# Revit family: BIM_KUBAIR F400 CC Pilotair Horizontal
name_source: partatom
category: Equipement de génie climatique
revit_build: Autodesk Revit 2016 (Build: 20161004_0715(x64)
units: mm (PartAtom-declared; Revit-internal decimal feet)

## family parameters
Basée sur le plan de construction = Non
Cote de connecteur circulaire = Utiliser le diamètre
Couper avec des vides une fois chargée = Non
Numéro OmniClass = 23.75.00.00
Partagée = Non
Point de calcul de pièce = Oui
Titre OmniClass = Climate Control (HVAC)
Toujours verticalement = Oui
Type d'élément = Normal

## types (68) — shared parameters
Classe_de_protection_electrique = F
Consignes – raccordements aérauliques = Raccorder 1, 2 ou 3 ouies  au refoulement et 1, 2 ou 3 ouies à l’aspiration
Fabricant = VIM
Hauteur_support = 30 mm  [stored 0.0984252 ft]
IfcExportAs = IfcFan
IfcExportType = IfcFlowMovingDevice
Lien_page_produit = http://www.vim.fr
Materiau_caisson = Acier, galvanisé
Materiau_support = Acier
Protection_IP = IP 55
Visibilité_marque = Oui

## per-type parameters (varying)
| type | A | BH | C | Code_article | Cote_A_capot | Cote_B_capot | Cote_C_capot | Courant_nominal | D | Debit_maxi | Debit_mini | EC | F | Hauteur_pilotair | J | KC | Largeur_pilotair | Modèle | Nombre_de_phases | Poids | Position_V_pilotair | Profondeur_pilotair | Puissance_electrique | Tension_nominale |
| KUBAIR F400 CC 355 4PM DP1M INTZ BDEZ 0,25kW Horizontal | 627 mm  [stored 2.05709 ft] | 695 mm  [stored 2.28018 ft] | 263 mm  [stored 0.862861 ft] | 644535 + 660100 | 340 mm  [stored 1.11549 ft] | 325 mm  [stored 1.06627 ft] | 305 mm  [stored 1.00066 ft] | 3 A | 559 mm  [stored 1.83399 ft] | 3090 m³/h | 900 m³/h | 790 mm | 660 mm  [stored 2.16535 ft] | 214 mm  [stored 0.7021 ft] | 102 mm | 954 mm | 259 mm  [stored 0.849738 ft] | KUBAIR F400 CC 355 4PM DP1M INTZ BDEZ 0,25kW Caisson horizontal | 1 | 59 Kg | 295 mm  [stored 0.967848 ft] | 218 mm  [stored 0.715223 ft] | 250 W | 230 V |
| KUBAIR F400 CC 355 6PM DP1M INTZ BDEZ 0,18kW Horizontal | 627 mm  [stored 2.05709 ft] | 695 mm  [stored 2.28018 ft] | 263 mm  [stored 0.862861 ft] | 644539 + 660100 | 340 mm  [stored 1.11549 ft] | 325 mm  [stored 1.06627 ft] | 305 mm  [stored 1.00066 ft] | 2 A | 559 mm  [stored 1.83399 ft] | 2140 m³/h | 620 m³/h | 790 mm | 660 mm  [stored 2.16535 ft] | 214 mm  [stored 0.7021 ft] | 102 mm | 954 mm | 259 mm  [stored 0.849738 ft] | KUBAIR F400 CC 355 6PM DP1M INTZ BDEZ 0,18kW Caisson horizontal | 1 | 59 Kg | 295 mm  [stored 0.967848 ft] | 218 mm  [stored 0.715223 ft] | 180 W | 230 V |
| KUBAIR F400 CC 355 4PT IE1 DP1V INTZ BDEZ 0,25kW Horizontal | 627 mm  [stored 2.05709 ft] | 695 mm  [stored 2.28018 ft] | 263 mm  [stored 0.862861 ft] | 644543 + 660100 | 340 mm  [stored 1.11549 ft] | 325 mm  [stored 1.06627 ft] | 305 mm  [stored 1.00066 ft] | 1 A | 559 mm  [stored 1.83399 ft] | 3090 m³/h | 900 m³/h | 790 mm | 660 mm  [stored 2.16535 ft] | 214 mm  [stored 0.7021 ft] | 102 mm | 954 mm | 259 mm  [stored 0.849738 ft] | KUBAIR F400 CC 355 4PT IE1 DP1V INTZ BDEZ 0,25kW Caisson horizontal | 3 | 59 Kg | 295 mm  [stored 0.967848 ft] | 218 mm  [stored 0.715223 ft] | 250 W | 400 V |
| KUBAIR F400 CC 355 4PT IE2 DP1V INTZ BDEZ 0,25kW Horizontal | 627 mm  [stored 2.05709 ft] | 695 mm  [stored 2.28018 ft] | 263 mm  [stored 0.862861 ft] | 644547 + 660100 | 340 mm  [stored 1.11549 ft] | 325 mm  [stored 1.06627 ft] | 305 mm  [stored 1.00066 ft] | 1 A | 559 mm  [stored 1.83399 ft] | 3090 m³/h | 900 m³/h | 790 mm | 660 mm  [stored 2.16535 ft] | 214 mm  [stored 0.7021 ft] | 102 mm | 954 mm | 259 mm  [stored 0.849738 ft] | KUBAIR F400 CC 355 4PT IE2 DP1V INTZ BDEZ 0,25kW Caisson horizontal | 3 | 59 Kg | 295 mm  [stored 0.967848 ft] | 218 mm  [stored 0.715223 ft] | 250 W | 400 V |
| KUBAIR F400 CC 355 4PT IE3 DP1V INTZ BDEZ 0,25kW Horizontal | 627 mm  [stored 2.05709 ft] | 695 mm  [stored 2.28018 ft] | 263 mm  [stored 0.862861 ft] | 644551 + 660100 | 340 mm  [stored 1.11549 ft] | 325 mm  [stored 1.06627 ft] | 305 mm  [stored 1.00066 ft] | 1 A | 559 mm  [stored 1.83399 ft] | 3090 m³/h | 900 m³/h | 790 mm | 660 mm  [stored 2.16535 ft] | 214 mm  [stored 0.7021 ft] | 102 mm | 954 mm | 259 mm  [stored 0.849738 ft] | KUBAIR F400 CC 355 4PT IE3 DP1V INTZ BDEZ 0,25kW Caisson horizontal | 3 | 59 Kg | 295 mm  [stored 0.967848 ft] | 218 mm  [stored 0.715223 ft] | 250 W | 400 V |
| KUBAIR F400 CC 355 6PT IE1 DP1V INTZ BDEZ 0,18kW Horizontal | 627 mm  [stored 2.05709 ft] | 695 mm  [stored 2.28018 ft] | 263 mm  [stored 0.862861 ft] | 644555 + 660100 | 340 mm  [stored 1.11549 ft] | 325 mm  [stored 1.06627 ft] | 305 mm  [stored 1.00066 ft] | 1 A | 559 mm  [stored 1.83399 ft] | 2140 m³/h | 620 m³/h | 790 mm | 660 mm  [stored 2.16535 ft] | 214 mm  [stored 0.7021 ft] | 102 mm | 954 mm | 259 mm  [stored 0.849738 ft] | KUBAIR F400 CC 355 6PT IE1 DP1V INTZ BDEZ 0,18kW Caisson horizontal | 3 | 59 Kg | 295 mm  [stored 0.967848 ft] | 218 mm  [stored 0.715223 ft] | 180 W | 400 V |
| KUBAIR F400 CC 355 6PT IE2 DP1V INTZ BDEZ 0,18kW Horizontal | 627 mm  [stored 2.05709 ft] | 695 mm  [stored 2.28018 ft] | 263 mm  [stored 0.862861 ft] | 644559 + 660100 | 340 mm  [stored 1.11549 ft] | 325 mm  [stored 1.06627 ft] | 305 mm  [stored 1.00066 ft] | 1 A | 559 mm  [stored 1.83399 ft] | 2140 m³/h | 620 m³/h | 790 mm | 660 mm  [stored 2.16535 ft] | 214 mm  [stored 0.7021 ft] | 102 mm | 954 mm | 259 mm  [stored 0.849738 ft] | KUBAIR F400 CC 355 6PT IE2 DP1V INTZ BDEZ 0,18kW Caisson horizontal | 3 | 59 Kg | 295 mm  [stored 0.967848 ft] | 218 mm  [stored 0.715223 ft] | 180 W | 400 V |
| KUBAIR F400 CC 355 6PT IE3 DP1V INTZ BDEZ 0,18kW Horizontal | 627 mm  [stored 2.05709 ft] | 695 mm  [stored 2.28018 ft] | 263 mm  [stored 0.862861 ft] | 644563 + 660100 | 340 mm  [stored 1.11549 ft] | 325 mm  [stored 1.06627 ft] | 305 mm  [stored 1.00066 ft] | 1 A | 559 mm  [stored 1.83399 ft] | 2140 m³/h | 620 m³/h | 790 mm | 660 mm  [stored 2.16535 ft] | 214 mm  [stored 0.7021 ft] | 102 mm | 954 mm | 259 mm  [stored 0.849738 ft] | KUBAIR F400 CC 355 6PT IE3 DP1V INTZ BDEZ 0,18kW Caisson horizontal | 3 | 59 Kg | 295 mm  [stored 0.967848 ft] | 218 mm  [stored 0.715223 ft] | 180 W | 400 V |
| KUBAIR F400 CC 400 4PM DP1M INTZ BDEZ 0,55kW Horizontal | 699 mm  [stored 2.29331 ft] | 767 mm  [stored 2.5164 ft] | 297 mm  [stored 0.974409 ft] | 644575 + 660101 | 340 mm  [stored 1.11549 ft] | 325 mm  [stored 1.06627 ft] | 305 mm  [stored 1.00066 ft] | 4 A | 631 mm  [stored 2.07021 ft] | 5000 m³/h | 1060 m³/h | 864 mm | 732 mm | 214 mm  [stored 0.7021 ft] | 102 mm | 1022 mm | 259 mm  [stored 0.849738 ft] | KUBAIR F400 CC 400 4PM DP1M INTZ BDEZ 0,55kW Caisson horizontal | 1 | 72 Kg | 295 mm  [stored 0.967848 ft] | 218 mm  [stored 0.715223 ft] | 550 W | 230 V |
| KUBAIR F400 CC 400 6PM DP1M INTZ BDEZ 0,25kW Horizontal | 699 mm  [stored 2.29331 ft] | 767 mm  [stored 2.5164 ft] | 297 mm  [stored 0.974409 ft] | 644579 + 660101 | 340 mm  [stored 1.11549 ft] | 325 mm  [stored 1.06627 ft] | 305 mm  [stored 1.00066 ft] | 2 A | 631 mm  [stored 2.07021 ft] | 3310 m³/h | 520 m³/h | 864 mm | 732 mm | 214 mm  [stored 0.7021 ft] | 102 mm | 1022 mm | 259 mm  [stored 0.849738 ft] | KUBAIR F400 CC 400 6PM DP1M INTZ BDEZ 0,25kW Caisson horizontal | 1 | 72 Kg | 295 mm  [stored 0.967848 ft] | 218 mm  [stored 0.715223 ft] | 250 W | 230 V |
| KUBAIR F400 CC 400 4PT IE1 DP1V INTZ BDEZ 0,55kW Horizontal | 699 mm  [stored 2.29331 ft] | 767 mm  [stored 2.5164 ft] | 297 mm  [stored 0.974409 ft] | 644583 + 660101 | 340 mm  [stored 1.11549 ft] | 325 mm  [stored 1.06627 ft] | 305 mm  [stored 1.00066 ft] | 1 A | 631 mm  [stored 2.07021 ft] | 5000 m³/h | 1060 m³/h | 864 mm | 732 mm | 214 mm  [stored 0.7021 ft] | 102 mm | 1022 mm | 259 mm  [stored 0.849738 ft] | KUBAIR F400 CC 400 4PT IE1 DP1V INTZ BDEZ 0,55kW Caisson horizontal | 3 | 72 Kg | 295 mm  [stored 0.967848 ft] | 218 mm  [stored 0.715223 ft] | 550 W | 400 V |
| KUBAIR F400 CC 400 4PT IE2 DP1V INTZ BDEZ 0,55kW Horizontal | 699 mm  [stored 2.29331 ft] | 767 mm  [stored 2.5164 ft] | 297 mm  [stored 0.974409 ft] | 644587 + 660101 | 340 mm  [stored 1.11549 ft] | 325 mm  [stored 1.06627 ft] | 305 mm  [stored 1.00066 ft] | 1 A | 631 mm  [stored 2.07021 ft] | 5000 m³/h | 1060 m³/h | 864 mm | 732 mm | 214 mm  [stored 0.7021 ft] | 102 mm | 1022 mm | 259 mm  [stored 0.849738 ft] | KUBAIR F400 CC 400 4PT IE2 DP1V INTZ BDEZ 0,55kW Caisson horizontal | 3 | 72 Kg | 295 mm  [stored 0.967848 ft] | 218 mm  [stored 0.715223 ft] | 550 W | 400 V |
| KUBAIR F400 CC 400 4PT IE3 DP1V INTZ BDEZ 0,55kW Horizontal | 699 mm  [stored 2.29331 ft] | 767 mm  [stored 2.5164 ft] | 297 mm  [stored 0.974409 ft] | 644591 + 660101 | 340 mm  [stored 1.11549 ft] | 325 mm  [stored 1.06627 ft] | 305 mm  [stored 1.00066 ft] | 1 A | 631 mm  [stored 2.07021 ft] | 5000 m³/h | 1060 m³/h | 864 mm | 732 mm | 214 mm  [stored 0.7021 ft] | 102 mm | 1022 mm | 259 mm  [stored 0.849738 ft] | KUBAIR F400 CC 400 4PT IE3 DP1V INTZ BDEZ 0,55kW Caisson horizontal | 3 | 72 Kg | 295 mm  [stored 0.967848 ft] | 218 mm  [stored 0.715223 ft] | 550 W | 400 V |
| KUBAIR F400 CC 400 6PT IE1 DP1V INTZ BDEZ 0,37kW Horizontal | 699 mm  [stored 2.29331 ft] | 767 mm  [stored 2.5164 ft] | 297 mm  [stored 0.974409 ft] | 644595 + 660101 | 340 mm  [stored 1.11549 ft] | 325 mm  [stored 1.06627 ft] | 305 mm  [stored 1.00066 ft] | 1 A | 631 mm  [stored 2.07021 ft] | 3310 m³/h | 520 m³/h | 864 mm | 732 mm | 214 mm  [stored 0.7021 ft] | 102 mm | 1022 mm | 259 mm  [stored 0.849738 ft] | KUBAIR F400 CC 400 6PT IE1 DP1V INTZ BDEZ 0,37kW Caisson horizontal | 3 | 72 Kg | 295 mm  [stored 0.967848 ft] | 218 mm  [stored 0.715223 ft] | 370 W | 400 V |
| KUBAIR F400 CC 400 6PT IE2 DP1V INTZ BDEZ 0,37kW Horizontal | 699 mm  [stored 2.29331 ft] | 767 mm  [stored 2.5164 ft] | 297 mm  [stored 0.974409 ft] | 644599 + 660101 | 340 mm  [stored 1.11549 ft] | 325 mm  [stored 1.06627 ft] | 305 mm  [stored 1.00066 ft] | 1 A | 631 mm  [stored 2.07021 ft] | 3310 m³/h | 520 m³/h | 864 mm | 732 mm | 214 mm  [stored 0.7021 ft] | 102 mm | 1022 mm | 259 mm  [stored 0.849738 ft] | KUBAIR F400 CC 400 6PT IE2 DP1V INTZ BDEZ 0,37kW Caisson horizontal | 3 | 72 Kg | 295 mm  [stored 0.967848 ft] | 218 mm  [stored 0.715223 ft] | 370 W | 400 V |
| KUBAIR F400 CC 400 6PT IE3 DP1V INTZ BDEZ 0,37kW Horizontal | 699 mm  [stored 2.29331 ft] | 767 mm  [stored 2.5164 ft] | 297 mm  [stored 0.974409 ft] | 644603 + 660101 | 340 mm  [stored 1.11549 ft] | 325 mm  [stored 1.06627 ft] | 305 mm  [stored 1.00066 ft] | 1 A | 631 mm  [stored 2.07021 ft] | 3310 m³/h | 520 m³/h | 864 mm | 732 mm | 214 mm  [stored 0.7021 ft] | 102 mm | 1022 mm | 259 mm  [stored 0.849738 ft] | KUBAIR F400 CC 400 6PT IE3 DP1V INTZ BDEZ 0,37kW Caisson horizontal | 3 | 72 Kg | 295 mm  [stored 0.967848 ft] | 218 mm  [stored 0.715223 ft] | 370 W | 400 V |
| KUBAIR F400 CC 450 6PM DP1M INTZ BDEZ 0,25kW Horizontal | 779 mm | 847 mm | 326 mm  [stored 1.06955 ft] | 644615 + 660102 | 340 mm  [stored 1.11549 ft] | 325 mm  [stored 1.06627 ft] | 305 mm  [stored 1.00066 ft] | 2 A | 711 mm  [stored 2.33268 ft] | 4750 m³/h | 820 m³/h | 990 mm | 812 mm | 214 mm  [stored 0.7021 ft] | 102 mm | 1081 mm | 259 mm  [stored 0.849738 ft] | KUBAIR F400 CC 450 6PM DP1M INTZ BDEZ 0,25kW Caisson horizontal | 1 | 92 Kg | 295 mm  [stored 0.967848 ft] | 218 mm  [stored 0.715223 ft] | 250 W | 230 V |
| KUBAIR F400 CC 450 4PT IE2 DP1V INTZ BDEZ 1,1kW Horizontal | 779 mm | 847 mm | 326 mm  [stored 1.06955 ft] | 644619 + 660102 | 340 mm  [stored 1.11549 ft] | 325 mm  [stored 1.06627 ft] | 305 mm  [stored 1.00066 ft] | 2 A | 711 mm  [stored 2.33268 ft] | 7080 m³/h | 1230 m³/h | 990 mm | 812 mm | 214 mm  [stored 0.7021 ft] | 102 mm | 1081 mm | 259 mm  [stored 0.849738 ft] | KUBAIR F400 CC 450 4PT IE2 DP1V INTZ BDEZ 1,1kW Caisson horizontal | 3 | 92 Kg | 295 mm  [stored 0.967848 ft] | 218 mm  [stored 0.715223 ft] | 1100 W | 400 V |
| KUBAIR F400 CC 450 4PT IE3 DP1V INTZ BDEZ 1,1kW Horizontal | 779 mm | 847 mm | 326 mm  [stored 1.06955 ft] | 644623 + 660102 | 340 mm  [stored 1.11549 ft] | 325 mm  [stored 1.06627 ft] | 305 mm  [stored 1.00066 ft] | 2 A | 711 mm  [stored 2.33268 ft] | 7080 m³/h | 1230 m³/h | 990 mm | 812 mm | 214 mm  [stored 0.7021 ft] | 102 mm | 1081 mm | 259 mm  [stored 0.849738 ft] | KUBAIR F400 CC 450 4PT IE3 DP1V INTZ BDEZ 1,1kW Caisson horizontal | 3 | 92 Kg | 295 mm  [stored 0.967848 ft] | 218 mm  [stored 0.715223 ft] | 1100 W | 400 V |
| KUBAIR F400 CC 450 6PT IE1 DP1V INTZ BDEZ 0,37kW Horizontal | 779 mm | 847 mm | 326 mm  [stored 1.06955 ft] | 644627 + 660102 | 340 mm  [stored 1.11549 ft] | 325 mm  [stored 1.06627 ft] | 305 mm  [stored 1.00066 ft] | 1 A | 711 mm  [stored 2.33268 ft] | 4750 m³/h | 820 m³/h | 990 mm | 812 mm | 214 mm  [stored 0.7021 ft] | 102 mm | 1081 mm | 259 mm  [stored 0.849738 ft] | KUBAIR F400 CC 450 6PT IE1 DP1V INTZ BDEZ 0,37kW Caisson horizontal | 3 | 92 Kg | 295 mm  [stored 0.967848 ft] | 218 mm  [stored 0.715223 ft] | 370 W | 400 V |
| KUBAIR F400 CC 450 6PT IE2 DP1V INTZ BDEZ 0,37kW Horizontal | 779 mm | 847 mm | 326 mm  [stored 1.06955 ft] | 644631 + 660102 | 340 mm  [stored 1.11549 ft] | 325 mm  [stored 1.06627 ft] | 305 mm  [stored 1.00066 ft] | 1 A | 711 mm  [stored 2.33268 ft] | 4750 m³/h | 820 m³/h | 990 mm | 812 mm | 214 mm  [stored 0.7021 ft] | 102 mm | 1081 mm | 259 mm  [stored 0.849738 ft] | KUBAIR F400 CC 450 6PT IE2 DP1V INTZ BDEZ 0,37kW Caisson horizontal | 3 | 92 Kg | 295 mm  [stored 0.967848 ft] | 218 mm  [stored 0.715223 ft] | 370 W | 400 V |
| KUBAIR F400 CC 450 6PT IE3 DP1V INTZ BDEZ 0,37kW Horizontal | 779 mm | 847 mm | 326 mm  [stored 1.06955 ft] | 644635 + 660102 | 340 mm  [stored 1.11549 ft] | 325 mm  [stored 1.06627 ft] | 305 mm  [stored 1.00066 ft] | 1 A | 711 mm  [stored 2.33268 ft] | 4750 m³/h | 820 m³/h | 990 mm | 812 mm | 214 mm  [stored 0.7021 ft] | 102 mm | 1081 mm | 259 mm  [stored 0.849738 ft] | KUBAIR F400 CC 450 6PT IE3 DP1V INTZ BDEZ 0,37kW Caisson horizontal | 3 | 92 Kg | 295 mm  [stored 0.967848 ft] | 218 mm  [stored 0.715223 ft] | 370 W | 400 V |
| KUBAIR F400 CC 450 8PT IE1 DP1V INTZ BDEZ 0,18kW Horizontal | 779 mm | 847 mm | 326 mm  [stored 1.06955 ft] | 644639 + 660102 | 340 mm  [stored 1.11549 ft] | 325 mm  [stored 1.06627 ft] | 305 mm  [stored 1.00066 ft] | 1 A | 711 mm  [stored 2.33268 ft] | 3420 m³/h | 590 m³/h | 990 mm | 812 mm | 214 mm  [stored 0.7021 ft] | 102 mm | 1081 mm | 259 mm  [stored 0.849738 ft] | KUBAIR F400 CC 450 8PT IE1 DP1V INTZ BDEZ 0,18kW Caisson horizontal | 3 | 92 Kg | 295 mm  [stored 0.967848 ft] | 218 mm  [stored 0.715223 ft] | 180 W | 400 V |
| KUBAIR F400 CC 450 8PT IE2 DP1V INTZ BDEZ 0,18kW Horizontal | 779 mm | 847 mm | 326 mm  [stored 1.06955 ft] | 644643 + 660102 | 340 mm  [stored 1.11549 ft] | 325 mm  [stored 1.06627 ft] | 305 mm  [stored 1.00066 ft] | 1 A | 711 mm  [stored 2.33268 ft] | 3420 m³/h | 590 m³/h | 990 mm | 812 mm | 214 mm  [stored 0.7021 ft] | 102 mm | 1081 mm | 259 mm  [stored 0.849738 ft] | KUBAIR F400 CC 450 8PT IE2 DP1V INTZ BDEZ 0,18kW Caisson horizontal | 3 | 92 Kg | 295 mm  [stored 0.967848 ft] | 218 mm  [stored 0.715223 ft] | 180 W | 400 V |
| KUBAIR F400 CC 450 8PT IE3 DP1V INTZ BDEZ 0,18kW Horizontal | 779 mm | 847 mm | 326 mm  [stored 1.06955 ft] | 644647 + 660102 | 340 mm  [stored 1.11549 ft] | 325 mm  [stored 1.06627 ft] | 305 mm  [stored 1.00066 ft] | 1 A | 711 mm  [stored 2.33268 ft] | 3420 m³/h | 590 m³/h | 990 mm | 812 mm | 214 mm  [stored 0.7021 ft] | 102 mm | 1081 mm | 259 mm  [stored 0.849738 ft] | KUBAIR F400 CC 450 8PT IE3 DP1V INTZ BDEZ 0,18kW Caisson horizontal | 3 | 92 Kg | 295 mm  [stored 0.967848 ft] | 218 mm  [stored 0.715223 ft] | 180 W | 400 V |
| KUBAIR F400 CC 500 6PM DP1M INTZ BDEZ 0,37kW Horizontal | 858 mm | 925 mm | 338 mm  [stored 1.10892 ft] | 644663 + 660103 | 415 mm | 475 mm | 355 mm  [stored 1.1647 ft] | 3 A | 768 mm  [stored 2.51969 ft] | 5960 m³/h | 920 m³/h | 1039 mm | 890 mm | 214 mm  [stored 0.7021 ft] | 112 mm  [stored 0.367454 ft] | 1145 mm | 259 mm  [stored 0.849738 ft] | KUBAIR F400 CC 500 6PM DP1M INTZ BDEZ 0,37kW Caisson horizontal | 1 | 114 Kg | 303 mm | 218 mm  [stored 0.715223 ft] | 370 W | 230 V |
| KUBAIR F400 CC 500 4PT IE2 DP1V INTZ BDEZ 1,5kW Horizontal | 858 mm | 925 mm | 338 mm  [stored 1.10892 ft] | 644667 + 660103 | 415 mm | 475 mm | 355 mm  [stored 1.1647 ft] | 3 A | 768 mm  [stored 2.51969 ft] | 8850 m³/h | 1370 m³/h | 1039 mm | 890 mm | 214 mm  [stored 0.7021 ft] | 112 mm  [stored 0.367454 ft] | 1145 mm | 259 mm  [stored 0.849738 ft] | KUBAIR F400 CC 500 4PT IE2 DP1V INTZ BDEZ 1,5kW Caisson horizontal | 3 | 114 Kg | 303 mm | 218 mm  [stored 0.715223 ft] | 1500 W | 400 V |
| KUBAIR F400 CC 500 4PT IE3 DP1V INTZ BDEZ 1,5kW Horizontal | 858 mm | 925 mm | 338 mm  [stored 1.10892 ft] | 644671 + 660103 | 415 mm | 475 mm | 355 mm  [stored 1.1647 ft] | 3 A | 768 mm  [stored 2.51969 ft] | 8850 m³/h | 1370 m³/h | 1039 mm | 890 mm | 214 mm  [stored 0.7021 ft] | 112 mm  [stored 0.367454 ft] | 1145 mm | 259 mm  [stored 0.849738 ft] | KUBAIR F400 CC 500 4PT IE3 DP1V INTZ BDEZ 1,5kW Caisson horizontal | 3 | 114 Kg | 303 mm | 218 mm  [stored 0.715223 ft] | 1500 W | 400 V |
| KUBAIR F400 CC 500 6PT IE1 DP1V INTZ BDEZ 0,55kW Horizontal | 858 mm | 925 mm | 338 mm  [stored 1.10892 ft] | 644675 + 660103 | 415 mm | 475 mm | 355 mm  [stored 1.1647 ft] | 2 A | 768 mm  [stored 2.51969 ft] | 5960 m³/h | 920 m³/h | 1039 mm | 890 mm | 214 mm  [stored 0.7021 ft] | 112 mm  [stored 0.367454 ft] | 1145 mm | 259 mm  [stored 0.849738 ft] | KUBAIR F400 CC 500 6PT IE1 DP1V INTZ BDEZ 0,55kW Caisson horizontal | 3 | 114 Kg | 303 mm | 218 mm  [stored 0.715223 ft] | 550 W | 400 V |
| KUBAIR F400 CC 500 6PT IE2 DP1V INTZ BDEZ 0,55kW Horizontal | 858 mm | 925 mm | 338 mm  [stored 1.10892 ft] | 644679 + 660103 | 415 mm | 475 mm | 355 mm  [stored 1.1647 ft] | 1 A | 768 mm  [stored 2.51969 ft] | 5960 m³/h | 920 m³/h | 1039 mm | 890 mm | 214 mm  [stored 0.7021 ft] | 112 mm  [stored 0.367454 ft] | 1145 mm | 259 mm  [stored 0.849738 ft] | KUBAIR F400 CC 500 6PT IE2 DP1V INTZ BDEZ 0,55kW Caisson horizontal | 3 | 114 Kg | 303 mm | 218 mm  [stored 0.715223 ft] | 550 W | 400 V |
| KUBAIR F400 CC 500 6PT IE3 DP1V INTZ BDEZ 0,55kW Horizontal | 858 mm | 925 mm | 338 mm  [stored 1.10892 ft] | 644683 + 660103 | 415 mm | 475 mm | 355 mm  [stored 1.1647 ft] | 1 A | 768 mm  [stored 2.51969 ft] | 5960 m³/h | 920 m³/h | 1039 mm | 890 mm | 214 mm  [stored 0.7021 ft] | 112 mm  [stored 0.367454 ft] | 1145 mm | 259 mm  [stored 0.849738 ft] | KUBAIR F400 CC 500 6PT IE3 DP1V INTZ BDEZ 0,55kW Caisson horizontal | 3 | 114 Kg | 303 mm | 218 mm  [stored 0.715223 ft] | 550 W | 400 V |
| KUBAIR F400 CC 500 8PT IE1 DP1V INTZ BDEZ 0,18kW Horizontal | 858 mm | 925 mm | 338 mm  [stored 1.10892 ft] | 644687 + 660103 | 415 mm | 475 mm | 355 mm  [stored 1.1647 ft] | 1 A | 768 mm  [stored 2.51969 ft] | 4280 m³/h | 660 m³/h | 1039 mm | 890 mm | 214 mm  [stored 0.7021 ft] | 112 mm  [stored 0.367454 ft] | 1145 mm | 259 mm  [stored 0.849738 ft] | KUBAIR F400 CC 500 8PT IE1 DP1V INTZ BDEZ 0,18kW Caisson horizontal | 3 | 114 Kg | 303 mm | 218 mm  [stored 0.715223 ft] | 180 W | 400 V |
| KUBAIR F400 CC 500 8PT IE2 DP1V INTZ BDEZ 0,18kW Horizontal | 858 mm | 925 mm | 338 mm  [stored 1.10892 ft] | 644691 + 660103 | 415 mm | 475 mm | 355 mm  [stored 1.1647 ft] | 1 A | 768 mm  [stored 2.51969 ft] | 4280 m³/h | 660 m³/h | 1039 mm | 890 mm | 214 mm  [stored 0.7021 ft] | 112 mm  [stored 0.367454 ft] | 1145 mm | 259 mm  [stored 0.849738 ft] | KUBAIR F400 CC 500 8PT IE2 DP1V INTZ BDEZ 0,18kW Caisson horizontal | 3 | 114 Kg | 303 mm | 218 mm  [stored 0.715223 ft] | 180 W | 400 V |
| KUBAIR F400 CC 500 8PT IE3 DP1V INTZ BDEZ 0,18kW Horizontal | 858 mm | 925 mm | 338 mm  [stored 1.10892 ft] | 644695 + 660103 | 415 mm | 475 mm | 355 mm  [stored 1.1647 ft] | 1 A | 768 mm  [stored 2.51969 ft] | 4280 m³/h | 660 m³/h | 1039 mm | 890 mm | 214 mm  [stored 0.7021 ft] | 112 mm  [stored 0.367454 ft] | 1145 mm | 259 mm  [stored 0.849738 ft] | KUBAIR F400 CC 500 8PT IE3 DP1V INTZ BDEZ 0,18kW Caisson horizontal | 3 | 114 Kg | 303 mm | 218 mm  [stored 0.715223 ft] | 180 W | 400 V |
| KUBAIR F400 CC 500 4/6PT DP2I INTZ BDEZ 1,50/0,37kW Horizontal | 858 mm | 925 mm | 338 mm  [stored 1.10892 ft] | 644699 + 660103 | 415 mm | 475 mm | 355 mm  [stored 1.1647 ft] | 4 A | 768 mm  [stored 2.51969 ft] | 8850 m³/h | 1370 m³/h | 1039 mm | 890 mm | 214 mm  [stored 0.7021 ft] | 112 mm  [stored 0.367454 ft] | 1145 mm | 259 mm  [stored 0.849738 ft] | KUBAIR F400 CC 500 4/6PT DP2I INTZ BDEZ 1,50/0,37kW Caisson horizontal | 3 | 116 Kg | 303 mm | 218 mm  [stored 0.715223 ft] | 1500 W | 400 V |
| KUBAIR F400 CC 500 4/8PT DP2D INTZ BDEZ 1,60/0,40kW Horizontal | 858 mm | 925 mm | 338 mm  [stored 1.10892 ft] | 644703 + 660103 | 415 mm | 475 mm | 355 mm  [stored 1.1647 ft] | 4 A | 768 mm  [stored 2.51969 ft] | 8850 m³/h | 1370 m³/h | 1039 mm | 890 mm | 214 mm  [stored 0.7021 ft] | 112 mm  [stored 0.367454 ft] | 1145 mm | 259 mm  [stored 0.849738 ft] | KUBAIR F400 CC 500 4/8PT DP2D INTZ BDEZ 1,60/0,40kW Caisson horizontal | 3 | 116 Kg | 303 mm | 218 mm  [stored 0.715223 ft] | 1600 W | 400 V |
| KUBAIR F400 CC 500 6/8PT DP2I INTZ BDEZ 0,55/0,37kW Horizontal | 858 mm | 925 mm | 338 mm  [stored 1.10892 ft] | 644707 + 660103 | 415 mm | 475 mm | 355 mm  [stored 1.1647 ft] | 2 A | 768 mm  [stored 2.51969 ft] | 5960 m³/h | 920 m³/h | 1039 mm | 890 mm | 214 mm  [stored 0.7021 ft] | 112 mm  [stored 0.367454 ft] | 1145 mm | 259 mm  [stored 0.849738 ft] | KUBAIR F400 CC 500 6/8PT DP2I INTZ BDEZ 0,55/0,37kW Caisson horizontal | 3 | 116 Kg | 303 mm | 218 mm  [stored 0.715223 ft] | 550 W | 400 V |
| KUBAIR F400 CC 560 4PT IE2 DP1V INTZ BDEZ 2,2kW Horizontal | 954 mm | 1021 mm | 354 mm | 644711 + 660104 | 415 mm | 475 mm | 355 mm  [stored 1.1647 ft] | 5 A | 864 mm | 11330 m³/h | 1520 m³/h | 1139 mm | 986 mm | 214 mm  [stored 0.7021 ft] | 112 mm  [stored 0.367454 ft] | 1178 mm | 259 mm  [stored 0.849738 ft] | KUBAIR F400 CC 560 4PT IE2 DP1V INTZ BDEZ 2,2kW Caisson horizontal | 3 | 159 Kg | 303 mm | 218 mm  [stored 0.715223 ft] | 2200 W | 400 V |
| KUBAIR F400 CC 560 4PT IE3 DP1V INTZ BDEZ 2,2kW Horizontal | 954 mm | 1021 mm | 354 mm | 644715 + 660104 | 415 mm | 475 mm | 355 mm  [stored 1.1647 ft] | 5 A | 864 mm | 11330 m³/h | 1520 m³/h | 1139 mm | 986 mm | 214 mm  [stored 0.7021 ft] | 112 mm  [stored 0.367454 ft] | 1178 mm | 259 mm  [stored 0.849738 ft] | KUBAIR F400 CC 560 4PT IE3 DP1V INTZ BDEZ 2,2kW Caisson horizontal | 3 | 159 Kg | 303 mm | 218 mm  [stored 0.715223 ft] | 2200 W | 400 V |
| KUBAIR F400 CC 560 6PT IE2 DP1V INTZ BDEZ 0,75kW Horizontal | 954 mm | 1021 mm | 354 mm | 644719 + 660104 | 415 mm | 475 mm | 355 mm  [stored 1.1647 ft] | 2 A | 864 mm | 7630 m³/h | 1020 m³/h | 1139 mm | 986 mm | 214 mm  [stored 0.7021 ft] | 112 mm  [stored 0.367454 ft] | 1178 mm | 259 mm  [stored 0.849738 ft] | KUBAIR F400 CC 560 6PT IE2 DP1V INTZ BDEZ 0,75kW Caisson horizontal | 3 | 159 Kg | 303 mm | 218 mm  [stored 0.715223 ft] | 750 W | 400 V |
| KUBAIR F400 CC 560 6PT IE3 DP1V INTZ BDEZ 0,75kW Horizontal | 954 mm | 1021 mm | 354 mm | 644723 + 660104 | 415 mm | 475 mm | 355 mm  [stored 1.1647 ft] | 2 A | 864 mm | 7630 m³/h | 1020 m³/h | 1139 mm | 986 mm | 214 mm  [stored 0.7021 ft] | 112 mm  [stored 0.367454 ft] | 1178 mm | 259 mm  [stored 0.849738 ft] | KUBAIR F400 CC 560 6PT IE3 DP1V INTZ BDEZ 0,75kW Caisson horizontal | 3 | 159 Kg | 303 mm | 218 mm  [stored 0.715223 ft] | 750 W | 400 V |
| KUBAIR F400 CC 560 8PT IE1 DP1V INTZ BDEZ 0,37kW Horizontal | 954 mm | 1021 mm | 354 mm | 644727 + 660104 | 415 mm | 475 mm | 355 mm  [stored 1.1647 ft] | 1 A | 864 mm | 5490 m³/h | 740 m³/h | 1139 mm | 986 mm | 214 mm  [stored 0.7021 ft] | 112 mm  [stored 0.367454 ft] | 1178 mm | 259 mm  [stored 0.849738 ft] | KUBAIR F400 CC 560 8PT IE1 DP1V INTZ BDEZ 0,37kW Caisson horizontal | 3 | 159 Kg | 303 mm | 218 mm  [stored 0.715223 ft] | 370 W | 400 V |
| KUBAIR F400 CC 560 8PT IE2 DP1V INTZ BDEZ 0,37kW Horizontal | 954 mm | 1021 mm | 354 mm | 644731 + 660104 | 415 mm | 475 mm | 355 mm  [stored 1.1647 ft] | 1 A | 864 mm | 5490 m³/h | 740 m³/h | 1139 mm | 986 mm | 214 mm  [stored 0.7021 ft] | 112 mm  [stored 0.367454 ft] | 1178 mm | 259 mm  [stored 0.849738 ft] | KUBAIR F400 CC 560 8PT IE2 DP1V INTZ BDEZ 0,37kW Caisson horizontal | 3 | 159 Kg | 303 mm | 218 mm  [stored 0.715223 ft] | 370 W | 400 V |
| KUBAIR F400 CC 560 8PT IE3 DP1V INTZ BDEZ 0,37kW Horizontal | 954 mm | 1021 mm | 354 mm | 644735 + 660104 | 415 mm | 475 mm | 355 mm  [stored 1.1647 ft] | 1 A | 864 mm | 5490 m³/h | 740 m³/h | 1139 mm | 986 mm | 214 mm  [stored 0.7021 ft] | 112 mm  [stored 0.367454 ft] | 1178 mm | 259 mm  [stored 0.849738 ft] | KUBAIR F400 CC 560 8PT IE3 DP1V INTZ BDEZ 0,37kW Caisson horizontal | 3 | 159 Kg | 303 mm | 218 mm  [stored 0.715223 ft] | 370 W | 400 V |
| KUBAIR F400 CC 560 4/6PT DP2I INTZ BDEZ 2,20/0,70kW Horizontal | 954 mm | 1021 mm | 354 mm | 644739 + 660104 | 415 mm | 475 mm | 355 mm  [stored 1.1647 ft] | 5 A | 864 mm | 11330 m³/h | 1520 m³/h | 1139 mm | 986 mm | 214 mm  [stored 0.7021 ft] | 112 mm  [stored 0.367454 ft] | 1178 mm | 259 mm  [stored 0.849738 ft] | KUBAIR F400 CC 560 4/6PT DP2I INTZ BDEZ 2,20/0,70kW Caisson horizontal | 3 | 161 Kg | 303 mm | 218 mm  [stored 0.715223 ft] | 2200 W | 400 V |
| KUBAIR F400 CC 560 4/8PT DP2D INTZ BDEZ 2,20/0,55kW Horizontal | 954 mm | 1021 mm | 354 mm | 644743 + 660104 | 415 mm | 475 mm | 355 mm  [stored 1.1647 ft] | 5 A | 864 mm | 11330 m³/h | 1520 m³/h | 1139 mm | 986 mm | 214 mm  [stored 0.7021 ft] | 112 mm  [stored 0.367454 ft] | 1178 mm | 259 mm  [stored 0.849738 ft] | KUBAIR F400 CC 560 4/8PT DP2D INTZ BDEZ 2,20/0,55kW Caisson horizontal | 3 | 161 Kg | 303 mm | 218 mm  [stored 0.715223 ft] | 2200 W | 400 V |
| KUBAIR F400 CC 560 6/8PT DP2I INTZ BDEZ 0,75/0,37kW Horizontal | 954 mm | 1021 mm | 354 mm | 644747 + 660104 | 415 mm | 475 mm | 355 mm  [stored 1.1647 ft] | 2 A | 864 mm | 7630 m³/h | 1020 m³/h | 1139 mm | 986 mm | 214 mm  [stored 0.7021 ft] | 112 mm  [stored 0.367454 ft] | 1178 mm | 259 mm  [stored 0.849738 ft] | KUBAIR F400 CC 560 6/8PT DP2I INTZ BDEZ 0,75/0,37kW Caisson horizontal | 3 | 161 Kg | 303 mm | 218 mm  [stored 0.715223 ft] | 750 W | 400 V |
| KUBAIR F400 CC 630 6PT IE2 DP1V INTZ BDEZ 1,1kW Horizontal | 1066 mm | 1133 mm | 403 mm  [stored 1.32218 ft] | 644751 + 660105 | 415 mm | 475 mm | 355 mm  [stored 1.1647 ft] | 3 A | 977 mm | 10000 m³/h | 1150 m³/h | 1183 mm | 1098 mm | 214 mm  [stored 0.7021 ft] | 112 mm  [stored 0.367454 ft] | 1273 mm | 259 mm  [stored 0.849738 ft] | KUBAIR F400 CC 630 6PT IE2 DP1V INTZ BDEZ 1,1kW Caisson horizontal | 3 | 162 Kg | 303 mm | 218 mm  [stored 0.715223 ft] | 1100 W | 400 V |
| KUBAIR F400 CC 630 6PT IE3 DP1V INTZ BDEZ 1,1kW Horizontal | 1066 mm | 1133 mm | 403 mm  [stored 1.32218 ft] | 644755 + 660105 | 415 mm | 475 mm | 355 mm  [stored 1.1647 ft] | 3 A | 977 mm | 10000 m³/h | 1150 m³/h | 1183 mm | 1098 mm | 214 mm  [stored 0.7021 ft] | 112 mm  [stored 0.367454 ft] | 1273 mm | 259 mm  [stored 0.849738 ft] | KUBAIR F400 CC 630 6PT IE3 DP1V INTZ BDEZ 1,1kW Caisson horizontal | 3 | 162 Kg | 303 mm | 218 mm  [stored 0.715223 ft] | 1100 W | 400 V |
| KUBAIR F400 CC 630 8PT IE1 DP1V INTZ BDEZ 0,55kW Horizontal | 1066 mm | 1133 mm | 403 mm  [stored 1.32218 ft] | 644759 + 660105 | 415 mm | 475 mm | 355 mm  [stored 1.1647 ft] | 2 A | 977 mm | 7270 m³/h | 860 m³/h | 1183 mm | 1098 mm | 214 mm  [stored 0.7021 ft] | 112 mm  [stored 0.367454 ft] | 1273 mm | 259 mm  [stored 0.849738 ft] | KUBAIR F400 CC 630 8PT IE1 DP1V INTZ BDEZ 0,55kW Caisson horizontal | 3 | 163 Kg | 303 mm | 218 mm  [stored 0.715223 ft] | 550 W | 400 V |
| KUBAIR F400 CC 630 8PT IE2 DP1V INTZ BDEZ 0,55kW Horizontal | 1066 mm | 1133 mm | 403 mm  [stored 1.32218 ft] | 644763 + 660105 | 415 mm | 475 mm | 355 mm  [stored 1.1647 ft] | 2 A | 977 mm | 7270 m³/h | 860 m³/h | 1183 mm | 1098 mm | 214 mm  [stored 0.7021 ft] | 112 mm  [stored 0.367454 ft] | 1273 mm | 259 mm  [stored 0.849738 ft] | KUBAIR F400 CC 630 8PT IE2 DP1V INTZ BDEZ 0,55kW Caisson horizontal | 3 | 163 Kg | 303 mm | 218 mm  [stored 0.715223 ft] | 550 W | 400 V |
| KUBAIR F400 CC 630 8PT IE3 DP1V INTZ BDEZ 0,55kW Horizontal | 1066 mm | 1133 mm | 403 mm  [stored 1.32218 ft] | 644767 + 660105 | 415 mm | 475 mm | 355 mm  [stored 1.1647 ft] | 2 A | 977 mm | 7270 m³/h | 860 m³/h | 1183 mm | 1098 mm | 214 mm  [stored 0.7021 ft] | 112 mm  [stored 0.367454 ft] | 1273 mm | 259 mm  [stored 0.849738 ft] | KUBAIR F400 CC 630 8PT IE3 DP1V INTZ BDEZ 0,55kW Caisson horizontal | 3 | 163 Kg | 303 mm | 218 mm  [stored 0.715223 ft] | 550 W | 400 V |
| KUBAIR F400 CC 630 6/8PT DP2I INTZ BDEZ 1,10/0,55kW Horizontal | 1066 mm | 1133 mm | 403 mm  [stored 1.32218 ft] | 644771 + 660105 | 415 mm | 475 mm | 355 mm  [stored 1.1647 ft] | 4 A | 977 mm | 10000 m³/h | 1150 m³/h | 1183 mm | 1098 mm | 214 mm  [stored 0.7021 ft] | 112 mm  [stored 0.367454 ft] | 1273 mm | 259 mm  [stored 0.849738 ft] | KUBAIR F400 CC 630 6/8PT DP2I INTZ BDEZ 1,10/0,55kW Caisson horizontal | 3 | 164 Kg | 303 mm | 218 mm  [stored 0.715223 ft] | 1100 W | 400 V |
| KUBAIR F400 CC 630 6/12PT DP2D INTZ BDEZ 1,10/0,22kW Horizontal | 1066 mm | 1133 mm | 403 mm  [stored 1.32218 ft] | 644775 + 660105 | 415 mm | 475 mm | 355 mm  [stored 1.1647 ft] | 4 A | 977 mm | 10000 m³/h | 1150 m³/h | 1183 mm | 1098 mm | 214 mm  [stored 0.7021 ft] | 112 mm  [stored 0.367454 ft] | 1273 mm | 259 mm  [stored 0.849738 ft] | KUBAIR F400 CC 630 6/12PT DP2D INTZ BDEZ 1,10/0,22kW Caisson horizontal | 3 | 164 Kg | 303 mm | 218 mm  [stored 0.715223 ft] | 1100 W | 400 V |
| KUBAIR F400 CC 710 6PT IE2 DP1V INTZ BDEZ 3,0kW Horizontal | 1194 mm | 1261 mm | 462 mm  [stored 1.51575 ft] | 644779 + 660106 | 510 mm  [stored 1.67323 ft] | 465 mm  [stored 1.52559 ft] | 450 mm  [stored 1.47638 ft] | 7 A | 1104 mm | 18900 m³/h | 420 m³/h | 1325 mm | 1226 mm | 299 mm  [stored 0.980971 ft] | 112 mm  [stored 0.367454 ft] | 1488 mm | 367 mm  [stored 1.20407 ft] | KUBAIR F400 CC 710 6PT IE2 DP1V INTZ BDEZ 3,0kW Caisson horizontal | 3 | 264 Kg | 435 mm  [stored 1.42717 ft] | 318 mm  [stored 1.04331 ft] | 3000 W | 400 V |
| KUBAIR F400 CC 710 6PT IE3 DP1V INTZ BDEZ 3,0kW Horizontal | 1194 mm | 1261 mm | 462 mm  [stored 1.51575 ft] | 644783 + 660106 | 510 mm  [stored 1.67323 ft] | 465 mm  [stored 1.52559 ft] | 450 mm  [stored 1.47638 ft] | 7 A | 1104 mm | 18900 m³/h | 420 m³/h | 1325 mm | 1226 mm | 299 mm  [stored 0.980971 ft] | 112 mm  [stored 0.367454 ft] | 1488 mm | 367 mm  [stored 1.20407 ft] | KUBAIR F400 CC 710 6PT IE3 DP1V INTZ BDEZ 3,0kW Caisson horizontal | 3 | 264 Kg | 435 mm  [stored 1.42717 ft] | 318 mm  [stored 1.04331 ft] | 3000 W | 400 V |
| KUBAIR F400 CC 710 8PT IE1 DP1V INTZ BDEZ 2,2kW Horizontal | 1194 mm | 1261 mm | 462 mm  [stored 1.51575 ft] | 644787 + 660106 | 510 mm  [stored 1.67323 ft] | 465 mm  [stored 1.52559 ft] | 450 mm  [stored 1.47638 ft] | 5 A | 1104 mm | 13600 m³/h | 300 m³/h | 1325 mm | 1226 mm | 299 mm  [stored 0.980971 ft] | 112 mm  [stored 0.367454 ft] | 1488 mm | 367 mm  [stored 1.20407 ft] | KUBAIR F400 CC 710 8PT IE1 DP1V INTZ BDEZ 2,2kW Caisson horizontal | 3 | 265 Kg | 435 mm  [stored 1.42717 ft] | 318 mm  [stored 1.04331 ft] | 2200 W | 400 V |
| KUBAIR F400 CC 710 8PT IE2 DP1V INTZ BDEZ 2,2kW Horizontal | 1194 mm | 1261 mm | 462 mm  [stored 1.51575 ft] | 644791 + 660106 | 510 mm  [stored 1.67323 ft] | 465 mm  [stored 1.52559 ft] | 450 mm  [stored 1.47638 ft] | 5 A | 1104 mm | 13600 m³/h | 300 m³/h | 1325 mm | 1226 mm | 299 mm  [stored 0.980971 ft] | 112 mm  [stored 0.367454 ft] | 1488 mm | 367 mm  [stored 1.20407 ft] | KUBAIR F400 CC 710 8PT IE2 DP1V INTZ BDEZ 2,2kW Caisson horizontal | 3 | 265 Kg | 435 mm  [stored 1.42717 ft] | 318 mm  [stored 1.04331 ft] | 2200 W | 400 V |
| KUBAIR F400 CC 710 8PT IE3 DP1V INTZ BDEZ 2,2kW Horizontal | 1194 mm | 1261 mm | 462 mm  [stored 1.51575 ft] | 644795 + 660106 | 510 mm  [stored 1.67323 ft] | 465 mm  [stored 1.52559 ft] | 450 mm  [stored 1.47638 ft] | 5 A | 1104 mm | 13600 m³/h | 300 m³/h | 1325 mm | 1226 mm | 299 mm  [stored 0.980971 ft] | 112 mm  [stored 0.367454 ft] | 1488 mm | 367 mm  [stored 1.20407 ft] | KUBAIR F400 CC 710 8PT IE3 DP1V INTZ BDEZ 2,2kW Caisson horizontal | 3 | 265 Kg | 435 mm  [stored 1.42717 ft] | 318 mm  [stored 1.04331 ft] | 2200 W | 400 V |
| KUBAIR F400 CC 710 6/8PT DP2I INTZ BDEZ 3,00/0,75kW Horizontal | 1194 mm | 1261 mm | 462 mm  [stored 1.51575 ft] | 644799 + 660106 | 510 mm  [stored 1.67323 ft] | 465 mm  [stored 1.52559 ft] | 450 mm  [stored 1.47638 ft] | 8 A | 1104 mm | 18900 m³/h | 420 m³/h | 1325 mm | 1226 mm | 299 mm  [stored 0.980971 ft] | 112 mm  [stored 0.367454 ft] | 1488 mm | 367 mm  [stored 1.20407 ft] | KUBAIR F400 CC 710 6/8PT DP2I INTZ BDEZ 3,00/0,75kW Caisson horizontal | 3 | 266 Kg | 435 mm  [stored 1.42717 ft] | 318 mm  [stored 1.04331 ft] | 3000 W | 400 V |
| KUBAIR F400 CC 710 6/12PT DP2D INTZ BDEZ 4,0/1,0kW Horizontal | 1194 mm | 1261 mm | 462 mm  [stored 1.51575 ft] | 644803 + 660106 | 510 mm  [stored 1.67323 ft] | 465 mm  [stored 1.52559 ft] | 450 mm  [stored 1.47638 ft] | 13 A | 1104 mm | 18900 m³/h | 420 m³/h | 1325 mm | 1226 mm | 299 mm  [stored 0.980971 ft] | 112 mm  [stored 0.367454 ft] | 1488 mm | 367 mm  [stored 1.20407 ft] | KUBAIR F400 CC 710 6/12PT DP2D INTZ BDEZ 4,0/1,0kW Caisson horizontal | 3 | 266 Kg | 435 mm  [stored 1.42717 ft] | 318 mm  [stored 1.04331 ft] | 4000 W | 400 V |
| KUBAIR F400 CC 800 6PT IE2 DP1V INTZ BDEZ 4,0kW Horizontal | 1338 mm | 1420 mm | 488 mm  [stored 1.60105 ft] | 644807 + 660107 | 510 mm  [stored 1.67323 ft] | 465 mm  [stored 1.52559 ft] | 450 mm  [stored 1.47638 ft] | 9 A | 1248 mm | 23390 m³/h | 660 m³/h | 1379 mm | 1370 mm | 299 mm  [stored 0.980971 ft] | 127 mm  [stored 0.416667 ft] | 1540 mm | 367 mm  [stored 1.20407 ft] | KUBAIR F400 CC 800 6PT IE2 DP1V INTZ BDEZ 4,0kW Caisson horizontal | 3 | 307 Kg | 435 mm  [stored 1.42717 ft] | 318 mm  [stored 1.04331 ft] | 4000 W | 400 V |
| KUBAIR F400 CC 800 6PT IE3 DP1V INTZ BDEZ 4,0kW Horizontal | 1338 mm | 1420 mm | 488 mm  [stored 1.60105 ft] | 644811 + 660107 | 510 mm  [stored 1.67323 ft] | 465 mm  [stored 1.52559 ft] | 450 mm  [stored 1.47638 ft] | 9 A | 1248 mm | 23390 m³/h | 660 m³/h | 1379 mm | 1370 mm | 299 mm  [stored 0.980971 ft] | 127 mm  [stored 0.416667 ft] | 1540 mm | 367 mm  [stored 1.20407 ft] | KUBAIR F400 CC 800 6PT IE3 DP1V INTZ BDEZ 4,0kW Caisson horizontal | 3 | 307 Kg | 435 mm  [stored 1.42717 ft] | 318 mm  [stored 1.04331 ft] | 4000 W | 400 V |
| KUBAIR F400 CC 800 8PT IE1 DP1V INTZ BDEZ 2,2kW Horizontal | 1338 mm | 1420 mm | 488 mm  [stored 1.60105 ft] | 644815 + 660107 | 510 mm  [stored 1.67323 ft] | 465 mm  [stored 1.52559 ft] | 450 mm  [stored 1.47638 ft] | 5 A | 1248 mm | 16910 m³/h | 480 m³/h | 1379 mm | 1370 mm | 299 mm  [stored 0.980971 ft] | 127 mm  [stored 0.416667 ft] | 1540 mm | 367 mm  [stored 1.20407 ft] | KUBAIR F400 CC 800 8PT IE1 DP1V INTZ BDEZ 2,2kW Caisson horizontal | 3 | 308 Kg | 435 mm  [stored 1.42717 ft] | 318 mm  [stored 1.04331 ft] | 2200 W | 400 V |
| KUBAIR F400 CC 800 8PT IE2 DP1V INTZ BDEZ 2,2kW Horizontal | 1338 mm | 1420 mm | 488 mm  [stored 1.60105 ft] | 644819 + 660107 | 510 mm  [stored 1.67323 ft] | 465 mm  [stored 1.52559 ft] | 450 mm  [stored 1.47638 ft] | 5 A | 1248 mm | 16910 m³/h | 480 m³/h | 1379 mm | 1370 mm | 299 mm  [stored 0.980971 ft] | 127 mm  [stored 0.416667 ft] | 1540 mm | 367 mm  [stored 1.20407 ft] | KUBAIR F400 CC 800 8PT IE2 DP1V INTZ BDEZ 2,2kW Caisson horizontal | 3 | 308 Kg | 435 mm  [stored 1.42717 ft] | 318 mm  [stored 1.04331 ft] | 2200 W | 400 V |
| KUBAIR F400 CC 800 8PT IE3 DP1V INTZ BDEZ 2,2kW Horizontal | 1338 mm | 1420 mm | 488 mm  [stored 1.60105 ft] | 644823 + 660107 | 510 mm  [stored 1.67323 ft] | 465 mm  [stored 1.52559 ft] | 450 mm  [stored 1.47638 ft] | 5 A | 1248 mm | 16910 m³/h | 480 m³/h | 1379 mm | 1370 mm | 299 mm  [stored 0.980971 ft] | 127 mm  [stored 0.416667 ft] | 1540 mm | 367 mm  [stored 1.20407 ft] | KUBAIR F400 CC 800 8PT IE3 DP1V INTZ BDEZ 2,2kW Caisson horizontal | 3 | 308 Kg | 435 mm  [stored 1.42717 ft] | 318 mm  [stored 1.04331 ft] | 2200 W | 400 V |
| KUBAIR F400 CC 800 6/8PT DP2I INTZ BDEZ 4,0/1,1kW Horizontal | 1338 mm | 1420 mm | 488 mm  [stored 1.60105 ft] | 644827 + 660107 | 510 mm  [stored 1.67323 ft] | 465 mm  [stored 1.52559 ft] | 450 mm  [stored 1.47638 ft] | 16 A | 1248 mm | 23390 m³/h | 660 m³/h | 1379 mm | 1370 mm | 299 mm  [stored 0.980971 ft] | 127 mm  [stored 0.416667 ft] | 1540 mm | 367 mm  [stored 1.20407 ft] | KUBAIR F400 CC 800 6/8PT DP2I INTZ BDEZ 4,0/1,1kW Caisson horizontal | 3 | 309 Kg | 435 mm  [stored 1.42717 ft] | 318 mm  [stored 1.04331 ft] | 4000 W | 400 V |
| KUBAIR F400 CC 800 6/12PT DP2D INTZ BDEZ 4,0/1,0kW Horizontal | 1338 mm | 1420 mm | 488 mm  [stored 1.60105 ft] | 644831 + 660107 | 510 mm  [stored 1.67323 ft] | 465 mm  [stored 1.52559 ft] | 450 mm  [stored 1.47638 ft] | 13 A | 1248 mm | 23390 m³/h | 660 m³/h | 1379 mm | 1370 mm | 299 mm  [stored 0.980971 ft] | 127 mm  [stored 0.416667 ft] | 1540 mm | 367 mm  [stored 1.20407 ft] | KUBAIR F400 CC 800 6/12PT DP2D INTZ BDEZ 4,0/1,0kW Caisson horizontal | 3 | 309 Kg | 435 mm  [stored 1.42717 ft] | 318 mm  [stored 1.04331 ft] | 4000 W | 400 V |

note: [stored X ft] marks values corroborated as IEEE doubles in the binary element streams (Revit-internal decimal feet)

## geometry (parser evidence)
native form markers: Blend x8
no freeform markers — native parametric forms only
